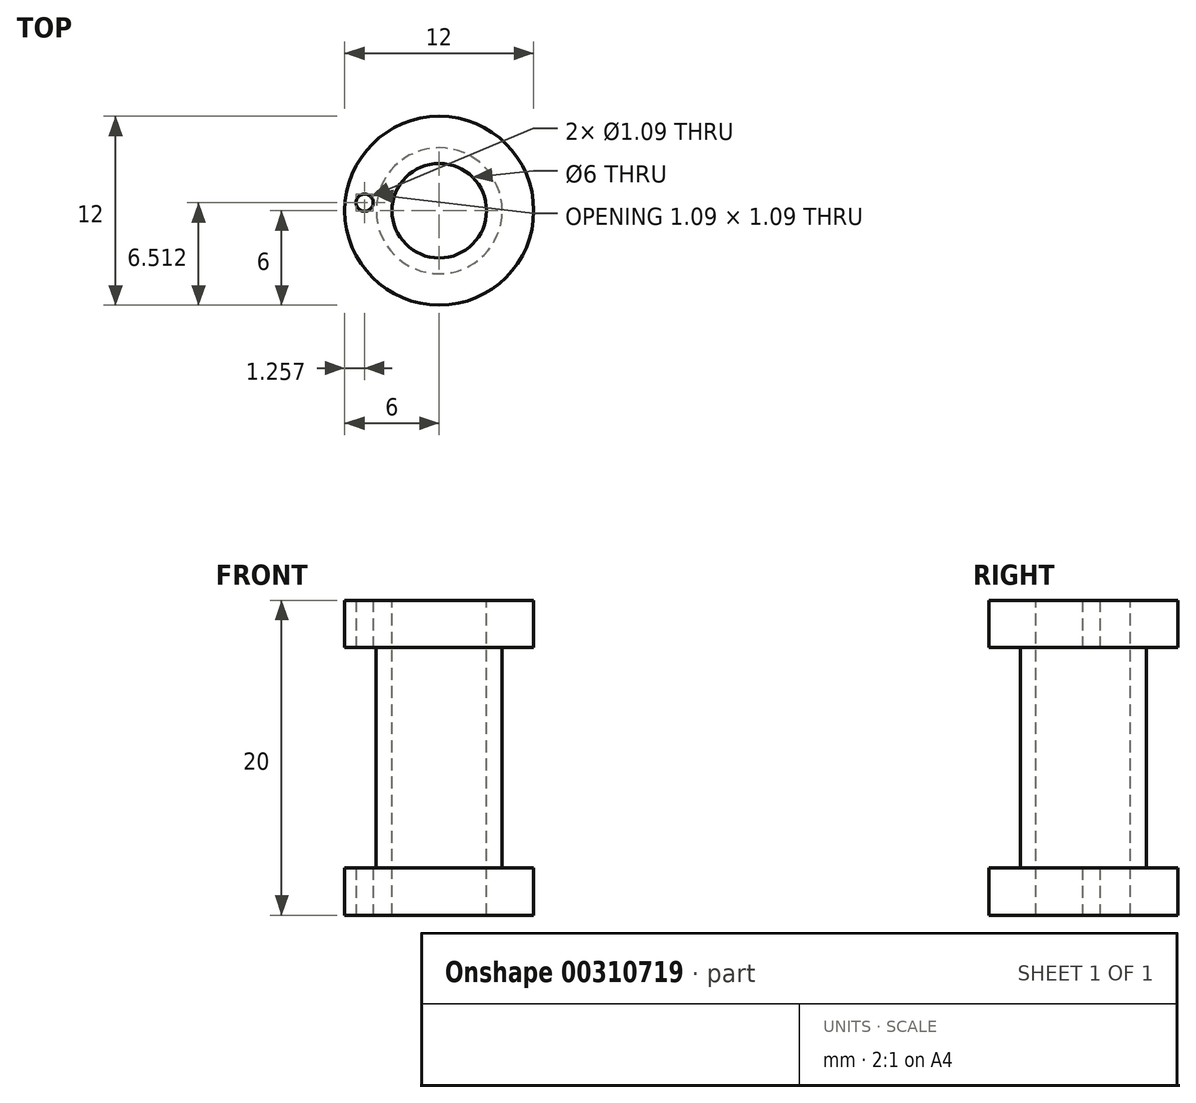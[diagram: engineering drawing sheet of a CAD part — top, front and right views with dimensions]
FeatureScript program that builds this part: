
annotation { "Feature Type Name" : "Feature", "Feature Type Description" : "" }
export const myFeature = defineFeature(function(context is Context, id is Id, definition is map)
    precondition{}
    {
        {
            var Q0;
            Q0=qCreatedBy(makeId("Front.planeOp"),FACE);
            var sketch = newSketch(context, id + "F0", { "sketchPlane" : qUnion([Q0])});
            skLineSegment(sketch, "E0", {"start": v(0, 19.92) * mm, "end": v(0, -16.62) * mm, "construction": true});
            skLineSegment(sketch, "E1", {"start": v(-3, 15.58) * mm, "end": v(-6, 15.58) * mm});
            skLineSegment(sketch, "E2", {"start": v(-6, 15.58) * mm, "end": v(-6, 12.58) * mm});
            skLineSegment(sketch, "E3", {"start": v(-6, 12.58) * mm, "end": v(-4, 12.58) * mm});
            skLineSegment(sketch, "E4", {"start": v(-4, 12.58) * mm, "end": v(-4, -1.42) * mm});
            skLineSegment(sketch, "E5", {"start": v(-4, -1.42) * mm, "end": v(-6, -1.42) * mm});
            skLineSegment(sketch, "E6", {"start": v(-6, -1.42) * mm, "end": v(-6, -4.42) * mm});
            skLineSegment(sketch, "E7", {"start": v(-6, -4.42) * mm, "end": v(-3, -4.42) * mm});
            skLineSegment(sketch, "E8", {"start": v(-3, -4.42) * mm, "end": v(-3, 15.58) * mm});
            skSolve(sketch);
        }
        {
            var Q0;
            Q0=makeQuery(id+"F0.imprint","IMPRINT",FACE,{"disambiguationData":[TD([[makeQuery(id+"F0.imprint","IMPRINT",EDGE,{"derivedFrom":sQuery(id+"F0.wireOp",EDGE,"E1")}),1.0]])]});
            var Q1;
            Q1=sQuery(id+"F0.wireOp",EDGE,"E0");
            revolve(context, id + "F1", {"entities" : qUnion([Q0]), "axis" : qUnion([Q1]), "revolveType" : RevolveType.FULL});
        }
        {
            var Q0;
            Q0=makeQuery(id+"F1.opRevolve","SWEPT_FACE",FACE,{"disambiguationData":[OSD([sQuery(id+"F0.wireOp",EDGE,"E5")])]});
            var sketch = newSketch(context, id + "F2", { "sketchPlane" : qUnion([Q0])});
            skCircle(sketch, "E9", {"center": v(-4.74, 0.51) * mm, "radius": 0.55 * mm});
            skSolve(sketch);
        }
        {
            var Q0;
            Q0 = qSketchRegion(id + "F2", true);
            extrude(context, id + "F3", {"entities" : qUnion([Q0]), "operationType" : NewBodyOperationType.REMOVE, "endBound" : BoundingType.SYMMETRIC, "depth" : 40.2 * mm});
        }
    });
